# Revit family: Malvestio_320800
name_source: partatom
category: Furniture
revit_build: Autodesk Revit Architecture 2014 (Build: 20131024_2115(x64)
units: mm (PartAtom-declared; Revit-internal decimal feet)

## types (1)
- Malvestio_320800
    BIMobject category = Other Furniture
    Date of publishing = 2014-10-30
    Depth = 780 mm  [stored 2.55906 ft]
    Description = Stretcher, runner range, hydraulically operated adjustable height on 2 columns, 2 section mattress platform in plastic laminate, trendelenburg/reverse trendelenburg, folding side rails, 5th wheel
    Design country = Italy
    Edition number = 1
    Height = 117 mm  [stored 0.383858 ft]
    IFC Classification = Furniture
    Installation instructions = http://www.malvestio.it
    Manufacturer country = Italy
    Manufacturer name = Malvestio
    Manufacturer url = http://www.malvestio.it
    Material Main = Plastic-Malvestio-320800-Laminated
    Material Secondary = Stainless-Malvestio-320800-Steel
    Nominal height = 117
    Nominal width = 2607
    Product SKU = STRETCHERS-320800
    Product data url = http://www.malvestio.it
    QR code = http://malvestio.bimobject.com
    UNSPSC Code = 56
    UNSPSC Name = Furniture and Furnishings
    URL = http://malvestio.bimobject.com
    Weight Net (Kg) = 0
    Width = 2607 mm  [stored 8.55315 ft]
    Youtube clip = http://www.malvestio.it

note: [stored X ft] marks values corroborated as IEEE doubles in the binary element streams (Revit-internal decimal feet)

## geometry (parser evidence)
native form markers: Sweep x3
no freeform markers — native parametric forms only
